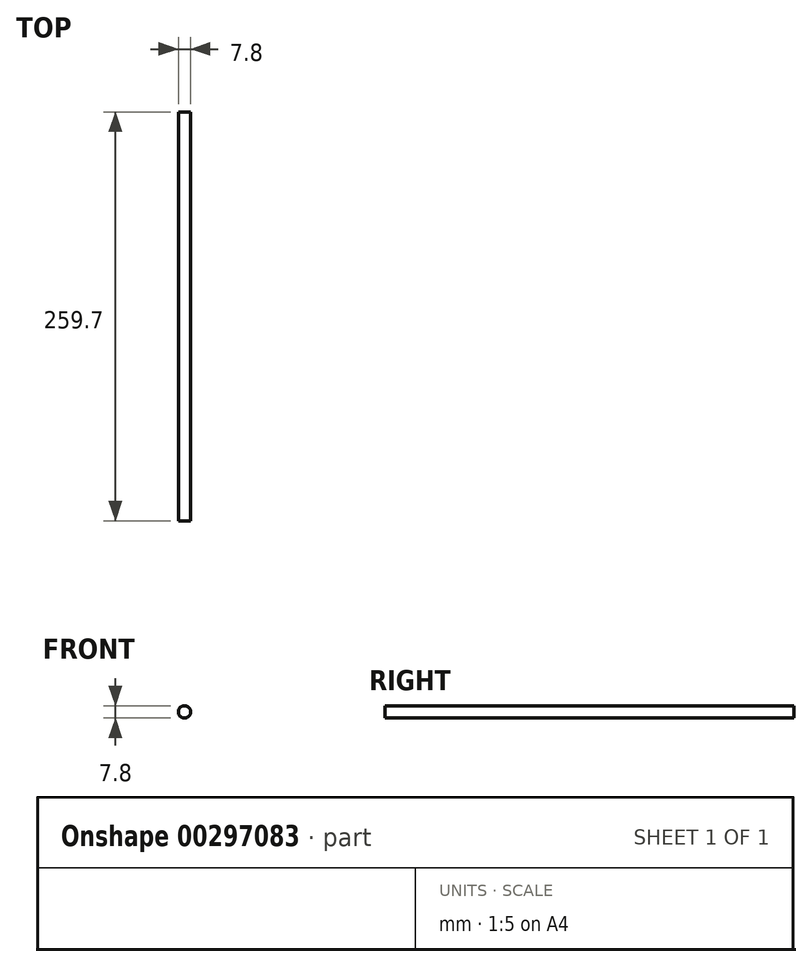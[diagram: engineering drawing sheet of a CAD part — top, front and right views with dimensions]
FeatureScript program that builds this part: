
annotation { "Feature Type Name" : "Feature", "Feature Type Description" : "" }
export const myFeature = defineFeature(function(context is Context, id is Id, definition is map)
    precondition{}
    {
        {
            var Q0;
            Q0=qCreatedBy(makeId("Front.planeOp"),FACE);
            var sketch = newSketch(context, id + "F0", { "sketchPlane" : qUnion([Q0])});
            skCircle(sketch, "E0", {"center": v(0, 0) * mm, "radius": 3.9 * mm});
            skSolve(sketch);
        }
        {
            var Q0;
            Q0 = qSketchRegion(id + "F0", true);
            extrude(context, id + "F1", {"entities" : qUnion([Q0]), "depth" : 259.7 * mm});
        }
    });
